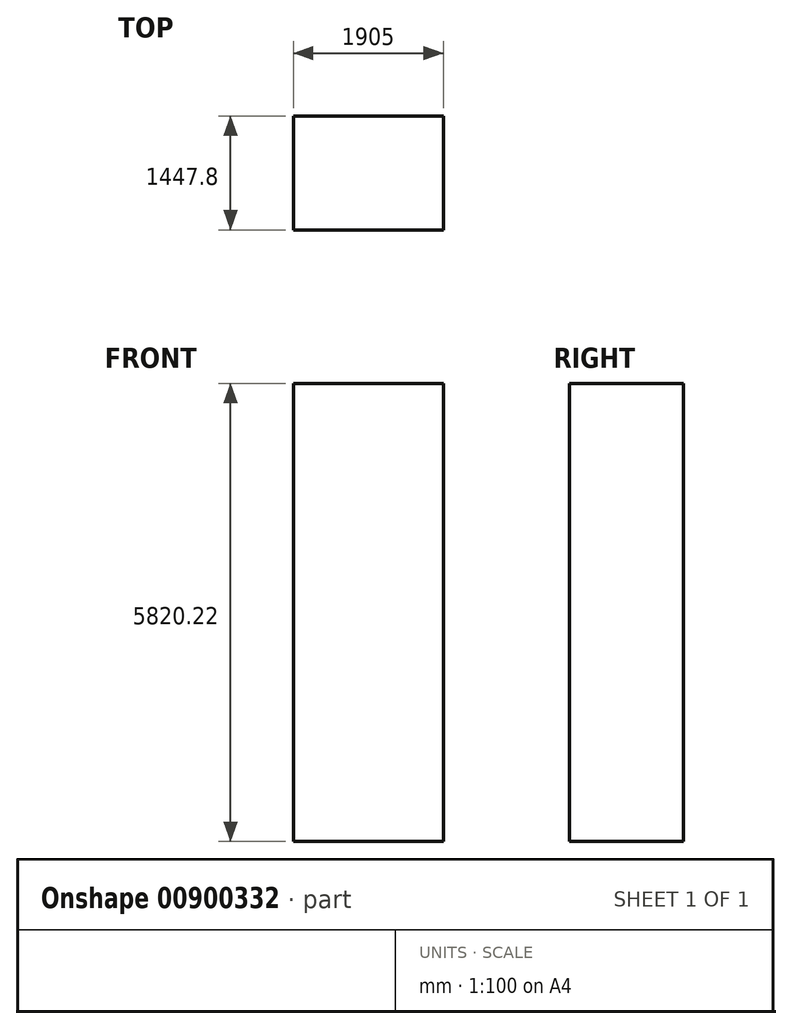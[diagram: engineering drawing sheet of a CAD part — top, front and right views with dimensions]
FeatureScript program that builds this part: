
annotation { "Feature Type Name" : "Feature", "Feature Type Description" : "" }
export const myFeature = defineFeature(function(context is Context, id is Id, definition is map)
    precondition{}
    {
        {
            var Q0;
            Q0=qCreatedBy(makeId("Top.planeOp"),FACE);
            var sketch = newSketch(context, id + "F0", { "sketchPlane" : qUnion([Q0])});
            skLineSegment(sketch, "E0.bottom", {"start": v(952.5, -723.9) * mm, "end": v(-952.5, -723.9) * mm});
            skLineSegment(sketch, "E0.top", {"start": v(952.5, 723.9) * mm, "end": v(-952.5, 723.9) * mm});
            skLineSegment(sketch, "E0.left", {"start": v(952.5, -723.9) * mm, "end": v(952.5, 723.9) * mm});
            skLineSegment(sketch, "E0.right", {"start": v(-952.5, -723.9) * mm, "end": v(-952.5, 723.9) * mm});
            skPoint(sketch, "E0.middle", {"position": v(0, 0) * mm});
            skSolve(sketch);
        }
        {
            var Q0;
            Q0=makeQuery(id+"F0.imprint","IMPRINT",FACE,{"disambiguationData":[TD([[makeQuery(id+"F0.imprint","IMPRINT",EDGE,{"derivedFrom":sQuery(id+"F0.wireOp",EDGE,"E0.bottom")}),-1.0]])]});
            extrude(context, id + "F1", {"entities" : qUnion([Q0]), "depth" : 25.4 * mm, "offsetDistance" : 25.4 * mm});
        }
        {
            var Q0;
            Q0=makeQuery(id+"F1.opExtrude","CAP_FACE",FACE,{"disambiguationData":[OSD([sQuery(id+"F0.wireOp",EDGE,"E0.bottom"),sQuery(id+"F0.wireOp",EDGE,"E0.top"),sQuery(id+"F0.wireOp",EDGE,"E0.left"),sQuery(id+"F0.wireOp",EDGE,"E0.right")])],"isStart":false});
            var sketch = newSketch(context, id + "F2", { "sketchPlane" : qUnion([Q0])});
            skSolve(sketch);
        }
        {
            var Q0;
            Q0=makeQuery(id+"F2.imprint","IMPRINT",FACE,{"disambiguationData":[TD([[makeQuery(id+"F2.imprint","IMPRINT",EDGE,{"derivedFrom":makeQuery(id+"F1.opExtrude","CAP_EDGE",EDGE,{"disambiguationData":[OSD([sQuery(id+"F0.wireOp",EDGE,"E0.bottom")])],"isStart":false})}),-1.0]])]});
            extrude(context, id + "F3", {"entities" : qUnion([Q0]), "operationType" : NewBodyOperationType.ADD, "endBound" : BoundingType.THROUGH_ALL, "depth" : 25.4 * mm, "offsetDistance" : 25.4 * mm});
        }
        {
            var Q0;
            {var subQ0=sQuery(id+"F0.wireOp",EDGE,"E0.left");Q0=makeQuery(id+"F3.boolean.opBoolean","MERGE",FACE,{"derivedFrom":[makeQuery(id+"F1.opExtrude","SWEPT_FACE",FACE,{"disambiguationData":[OSD([subQ0])]}),makeQuery(id+"F3.opExtrude","SWEPT_FACE",FACE,{"disambiguationData":[OSD([subQ0])]})]});}
            var sketch = newSketch(context, id + "F4", { "sketchPlane" : qUnion([Q0])});
            skSolve(sketch);
        }
        {
            var Q0;
            Q0=makeQuery(id+"F3.opExtrude","CAP_FACE",FACE,{"disambiguationData":[OSD([sQuery(id+"F0.wireOp",EDGE,"E0.bottom"),sQuery(id+"F0.wireOp",EDGE,"E0.top"),sQuery(id+"F0.wireOp",EDGE,"E0.left"),sQuery(id+"F0.wireOp",EDGE,"E0.right")])],"isStart":false});
            var sketch = newSketch(context, id + "F5", { "sketchPlane" : qUnion([Q0])});
            skSolve(sketch);
        }
        {
            var Q0;
            Q0=makeQuery(id+"F5.imprint","IMPRINT",FACE,{"disambiguationData":[TD([[makeQuery(id+"F5.imprint","IMPRINT",EDGE,{"derivedFrom":makeQuery(id+"F3.opExtrude","CAP_EDGE",EDGE,{"disambiguationData":[OSD([sQuery(id+"F0.wireOp",EDGE,"E0.bottom")])],"isStart":false})}),-1.0]])]});
            extrude(context, id + "F6", {"entities" : qUnion([Q0]), "operationType" : NewBodyOperationType.ADD, "endBound" : BoundingType.THROUGH_ALL, "depth" : 25.4 * mm, "offsetDistance" : 25.4 * mm});
        }
    });
